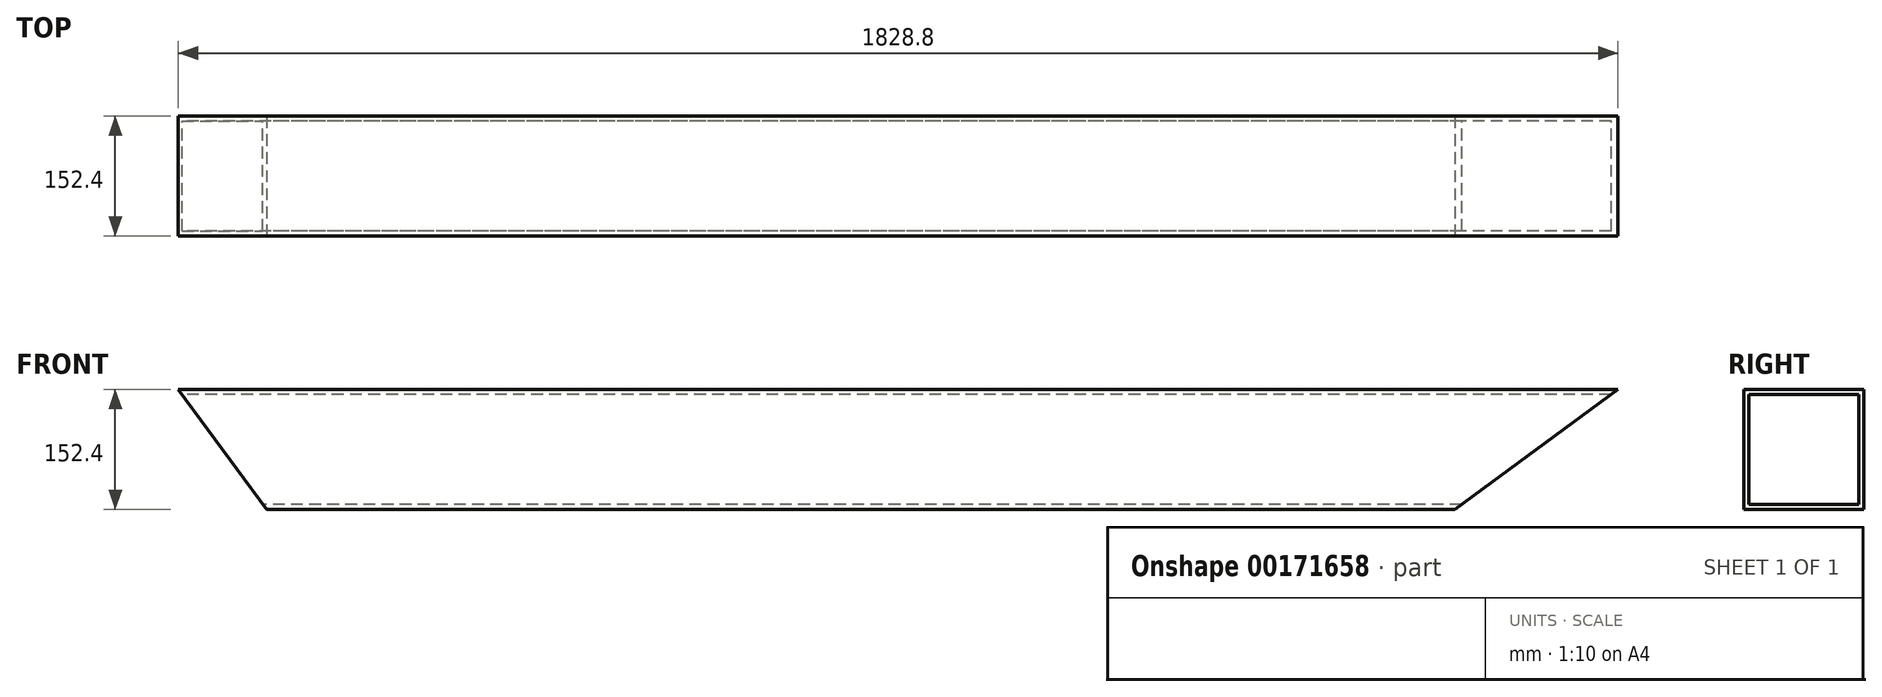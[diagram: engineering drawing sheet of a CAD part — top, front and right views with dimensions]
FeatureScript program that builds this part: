
annotation { "Feature Type Name" : "Feature", "Feature Type Description" : "" }
export const myFeature = defineFeature(function(context is Context, id is Id, definition is map)
    precondition{}
    {
        {
            var Q0;
            Q0=qCreatedBy(makeId("Right.planeOp"),FACE);
            var sketch = newSketch(context, id + "F0", { "sketchPlane" : qUnion([Q0])});
            skLineSegment(sketch, "E0.bottom", {"start": v(-76.2, 76.2) * mm, "end": v(76.2, 76.2) * mm});
            skLineSegment(sketch, "E0.top", {"start": v(-76.2, -76.2) * mm, "end": v(76.2, -76.2) * mm});
            skLineSegment(sketch, "E0.left", {"start": v(-76.2, 76.2) * mm, "end": v(-76.2, -76.2) * mm});
            skLineSegment(sketch, "E0.right", {"start": v(76.2, 76.2) * mm, "end": v(76.2, -76.2) * mm});
            skLineSegment(sketch, "E1.bottom", {"start": v(-69.85, 69.85) * mm, "end": v(69.85, 69.85) * mm});
            skLineSegment(sketch, "E1.top", {"start": v(-69.85, -69.85) * mm, "end": v(69.85, -69.85) * mm});
            skLineSegment(sketch, "E1.left", {"start": v(-69.85, 69.85) * mm, "end": v(-69.85, -69.85) * mm});
            skLineSegment(sketch, "E1.right", {"start": v(69.85, 69.85) * mm, "end": v(69.85, -69.85) * mm});
            skSolve(sketch);
        }
        {
            var Q0;
            Q0=makeQuery(id+"F0.imprint","IMPRINT",FACE,{"disambiguationData":[TD([[makeQuery(id+"F0.imprint","IMPRINT",EDGE,{"derivedFrom":sQuery(id+"F0.wireOp",EDGE,"E0.bottom")}),-1.0]])]});
            extrude(context, id + "F1", {"entities" : qUnion([Q0]), "depth" : 1828.8 * mm});
        }
        {
            var Q0;
            Q0=makeQuery(id+"F1.opExtrude","SWEPT_FACE",FACE,{"disambiguationData":[OSD([sQuery(id+"F0.wireOp",EDGE,"E0.left")])]});
            var sketch = newSketch(context, id + "F2", { "sketchPlane" : qUnion([Q0])});
            skLineSegment(sketch, "E2", {"start": v(0, 76.2) * mm, "end": v(0, -76.2) * mm});
            skLineSegment(sketch, "E3", {"start": v(0, -76.2) * mm, "end": v(112.11, -76.2) * mm});
            skLineSegment(sketch, "E4", {"start": v(112.11, -76.2) * mm, "end": v(0, 76.2) * mm});
            skLineSegment(sketch, "E5", {"start": v(1828.8, 76.2) * mm, "end": v(1828.8, -76.2) * mm});
            skPoint(sketch, "E5.startSnap0", {"position": v(1828.8, 0) * mm});
            skLineSegment(sketch, "E6", {"start": v(1828.8, -76.2) * mm, "end": v(1621.64, -76.2) * mm});
            skLineSegment(sketch, "E7", {"start": v(1621.64, -76.2) * mm, "end": v(1828.8, 76.2) * mm});
            skSolve(sketch);
        }
        {
            var Q0;
            Q0 = qSketchRegion(id + "F2", true);
            extrude(context, id + "F3", {"entities" : qUnion([Q0]), "operationType" : NewBodyOperationType.REMOVE, "oppositeDirection" : true, "depth" : 203.2 * mm});
        }
    });
